# Revit family: Mechanism_Kit-Mini_Column-Simon-500_CIMA
name_source: partatom
category: Electrical Fixtures
revit_build: Autodesk Revit 2014 (Build: 20130308_1515(x64)
units: mm (PartAtom-declared; Revit-internal decimal feet)

## types (1)
- 3 Modules, White
    Cost = 127.03€
    Current = 16 A
    Default Elevation = 1219 mm
    Description = UPS 1-face mini-column with 1 double Schuko outlet, 1 double UPS Schuko outlet and 2 V&D plates for 1 RJ45 connector
    Element Material = 9003 Signal white
    Manufacturer = SIMON
    Manufacturing material = Anodized aluminium
    Mini-Column Depth = 72 mm
    Overall dimensions = 451x110 mm
    Protection against impacts = IK08
    Protection against solid and liquid bodies = IP40
    RAL Color = 9003 Signal white
    RJ45 compatibility figure = Keystone I, II and Systimax
    Series = Simon 500 CIMA
    Technical data sheet = http://www.simon.es
    URL = http://www.simon.es
    Voice and data connectors type = RJ45

## geometry (parser evidence)
native form markers: Blend x2, Sweep x1
no freeform markers — native parametric forms only
